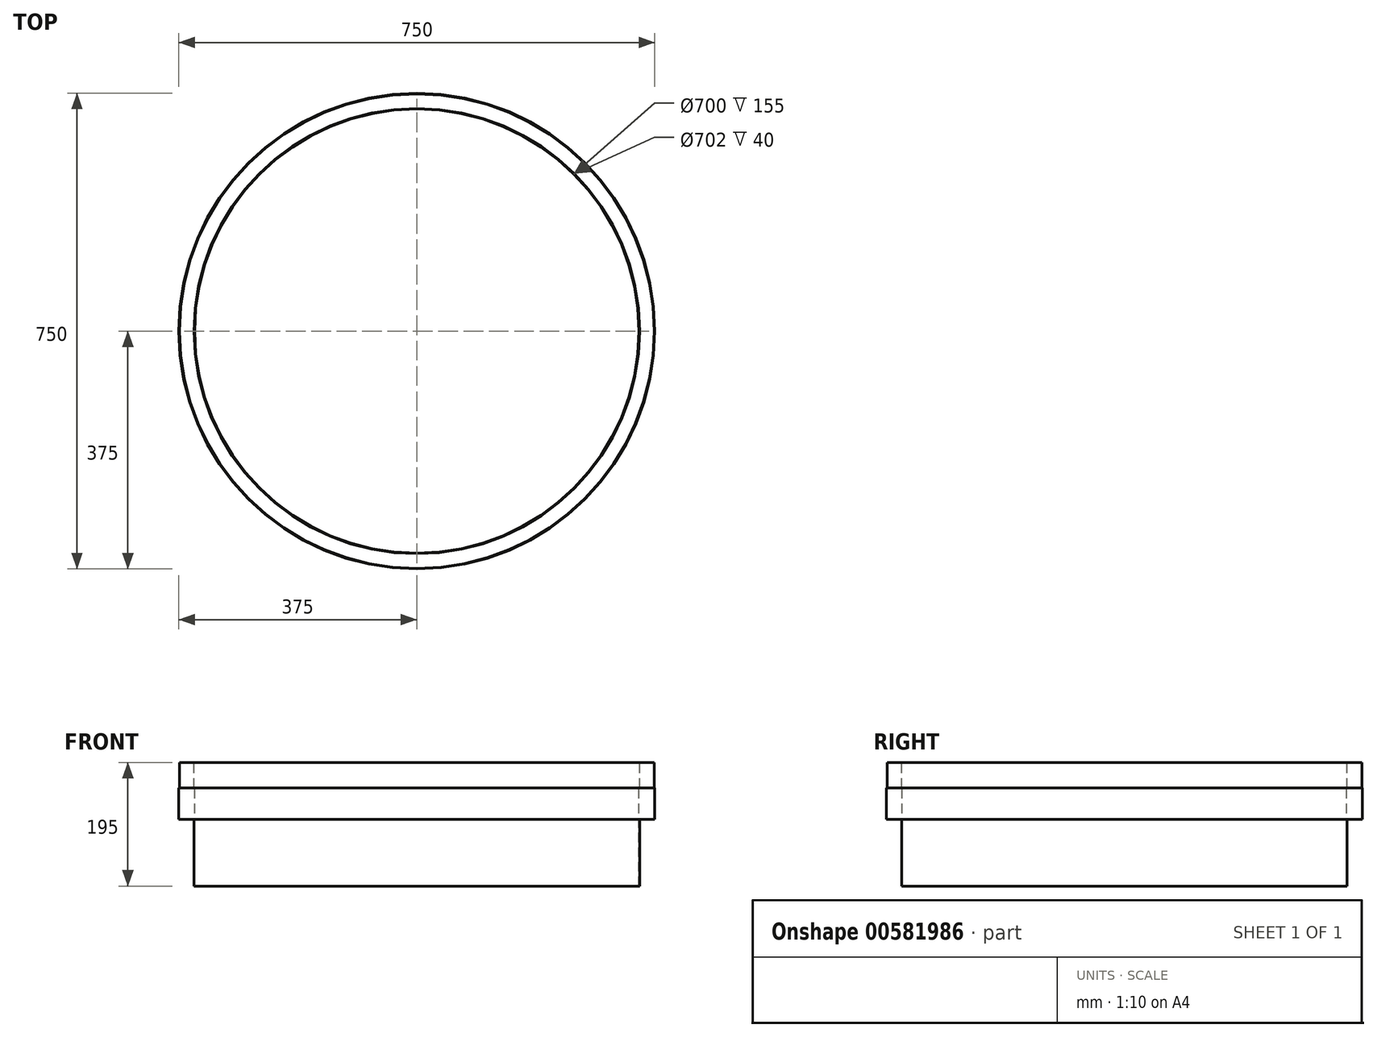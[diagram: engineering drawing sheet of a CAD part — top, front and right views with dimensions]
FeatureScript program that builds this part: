
annotation { "Feature Type Name" : "Feature", "Feature Type Description" : "" }
export const myFeature = defineFeature(function(context is Context, id is Id, definition is map)
    precondition{}
    {
        {
            var Q0;
            Q0=qCreatedBy(makeId("Front.planeOp"),FACE);
            var sketch = newSketch(context, id + "F0", { "sketchPlane" : qUnion([Q0])});
            skLineSegment(sketch, "E0", {"start": v(0, 710.75) * mm, "end": v(0, -704.58) * mm, "construction": true});
            skLineSegment(sketch, "E1", {"start": v(-350, 295.65) * mm, "end": v(-350, 410.65) * mm});
            skLineSegment(sketch, "E2", {"start": v(-350, 410.65) * mm, "end": v(-351, 410.65) * mm});
            skLineSegment(sketch, "E3", {"start": v(-374, 410.65) * mm, "end": v(-375, 410.65) * mm});
            skLineSegment(sketch, "E4", {"start": v(-375, 410.65) * mm, "end": v(-375, 360.65) * mm});
            skLineSegment(sketch, "E5", {"start": v(-375, 360.65) * mm, "end": v(-351, 360.65) * mm});
            skLineSegment(sketch, "E6", {"start": v(-351, 360.65) * mm, "end": v(-351, 295.65) * mm});
            skLineSegment(sketch, "E7", {"start": v(-374, 450.65) * mm, "end": v(-374, 410.65) * mm});
            skLineSegment(sketch, "E8", {"start": v(-374, 450.65) * mm, "end": v(-351, 450.65) * mm});
            skLineSegment(sketch, "E9", {"start": v(-351, 410.65) * mm, "end": v(-351, 450.65) * mm});
            skLineSegment(sketch, "E10", {"start": v(-350, 295.65) * mm, "end": v(-350, 255.65) * mm});
            skLineSegment(sketch, "E11", {"start": v(-351, 295.65) * mm, "end": v(-351, 255.65) * mm});
            skLineSegment(sketch, "E12", {"start": v(-351, 255.65) * mm, "end": v(-350, 255.65) * mm});
            skSolve(sketch);
        }
        {
            var Q0;
            Q0=qSketchRegion(id+"F0",true);
            var Q1;
            Q1=sQuery(id+"F0.wireOp",EDGE,"E0");
            revolve(context, id + "F1", {"entities" : qUnion([Q0]), "axis" : qUnion([Q1]), "revolveType" : RevolveType.FULL});
        }
    });
